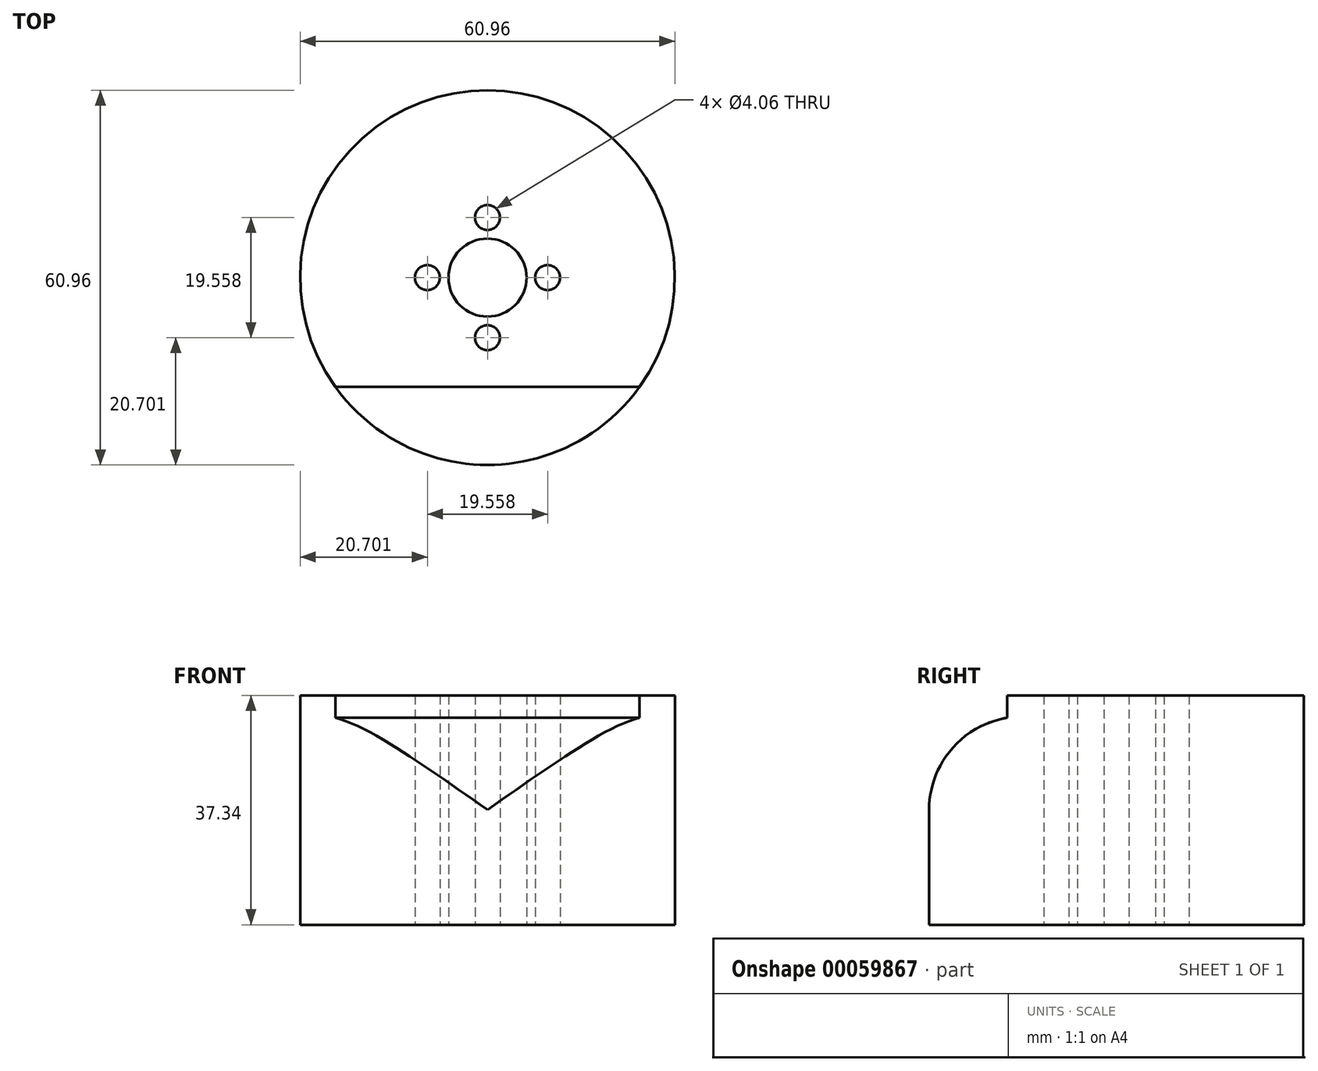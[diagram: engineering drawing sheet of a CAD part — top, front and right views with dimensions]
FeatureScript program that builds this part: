
annotation { "Feature Type Name" : "Feature", "Feature Type Description" : "" }
export const myFeature = defineFeature(function(context is Context, id is Id, definition is map)
    precondition{}
    {
        {
            var Q0;
            Q0=qCreatedBy(makeId("Top.planeOp"),FACE);
            var sketch = newSketch(context, id + "F0", { "sketchPlane" : qUnion([Q0])});
            skCircle(sketch, "E0", {"center": v(0, 0) * mm, "radius": 30.48 * mm});
            skCircle(sketch, "E1", {"center": v(0, 0) * mm, "radius": 6.35 * mm});
            skLineSegment(sketch, "E2", {"start": v(0, 0) * mm, "end": v(-9.78, 0) * mm});
            skLineSegment(sketch, "E3", {"start": v(0, 0) * mm, "end": v(9.78, 0) * mm});
            skLineSegment(sketch, "E4", {"start": v(0, 0) * mm, "end": v(0, -9.78) * mm});
            skLineSegment(sketch, "E5", {"start": v(0, 0) * mm, "end": v(0, 9.78) * mm});
            skCircle(sketch, "E6", {"center": v(-9.78, 0) * mm, "radius": 2.03 * mm});
            skCircle(sketch, "E7", {"center": v(0, 9.78) * mm, "radius": 2.03 * mm});
            skCircle(sketch, "E8", {"center": v(9.78, 0) * mm, "radius": 2.03 * mm});
            skCircle(sketch, "E9", {"center": v(0, -9.78) * mm, "radius": 2.03 * mm});
            skSolve(sketch);
        }
        {
            var Q0;
            Q0 = qSketchRegion(id + "F0", true);
            extrude(context, id + "F1", {"entities" : qUnion([Q0]), "depth" : 37.34 * mm});
        }
        {
            var Q0;
            Q0=qCreatedBy(makeId("Right.planeOp"),FACE);
            var sketch = newSketch(context, id + "F2", { "sketchPlane" : qUnion([Q0])});
            skPoint(sketch, "E10.endSnap0", {"position": v(5.2, -10.74) * mm});
            skLineSegment(sketch, "E10", {"start": v(5.2, -10.74) * mm, "end": v(17.9, -10.74) * mm});
            skLineSegment(sketch, "E11", {"start": v(5.2, 8.56) * mm, "end": v(5.2, 4.24) * mm});
            skLineSegment(sketch, "E12", {"start": v(5.2, 4.24) * mm, "end": v(5.2, -25.73) * mm});
            skLineSegment(sketch, "E13", {"start": v(0, 0) * mm, "end": v(-30.48, 0) * mm});
            skLineSegment(sketch, "E14", {"start": v(-30.48, 0) * mm, "end": v(-30.48, 37.4) * mm});
            skLineSegment(sketch, "E15", {"start": v(-30.48, 37.4) * mm, "end": v(0, 37.4) * mm});
            skLineSegment(sketch, "E16", {"start": v(-30.48, 18.7) * mm, "end": v(-17.78, 18.7) * mm});
            skPoint(sketch, "E16.endSnap0", {"position": v(-30.48, 18.7) * mm});
            skLineSegment(sketch, "E17", {"start": v(-17.78, 18.7) * mm, "end": v(-17.78, 33.68) * mm});
            skLineSegment(sketch, "E18", {"start": v(-17.78, 33.68) * mm, "end": v(-17.78, 3.71) * mm});
            skArc(sketch, "E19", {"start": v(-17.78, 33.68) * mm, "mid": v(-30.48, 18.7) * mm, "end": v(-17.78, 3.71) * mm});
            skLineSegment(sketch, "E20", {"start": v(-17.78, 33.68) * mm, "end": v(-17.78, 37.4) * mm});
            skLineSegment(sketch, "E21", {"start": v(-17.78, 37.4) * mm, "end": v(-30.48, 37.4) * mm});
            skLineSegment(sketch, "E22", {"start": v(-30.48, 0) * mm, "end": v(-17.78, 0) * mm});
            skLineSegment(sketch, "E23", {"start": v(-17.78, 0) * mm, "end": v(-17.78, 3.71) * mm});
            skSolve(sketch);
        }
        {
            var Q0;
            {var subQ4=sQuery(id+"F2.wireOp",EDGE,"E20");Q0=makeQuery(id+"F2.imprint","IMPRINT",FACE,{"disambiguationData":[TD([[makeQuery(id+"F2.imprint","IMPRINT",EDGE,{"derivedFrom":subQ4}),1.0]])]});}
            var Q1;
            {var subQ0=sQuery(id+"F2.wireOp",EDGE,"E22");Q1=makeQuery(id+"F2.imprint","IMPRINT",FACE,{"disambiguationData":[TD([[makeQuery(id+"F2.imprint","IMPRINT",EDGE,{"derivedFrom":subQ0}),1.0]])]});}
            extrude(context, id + "F3", {"entities" : qUnion([Q0, Q1]), "operationType" : NewBodyOperationType.REMOVE, "oppositeDirection" : true, "depth" : 39.58 * mm});
        }
        {
            var Q0;
            {var subQ4=sQuery(id+"F2.wireOp",EDGE,"E20");Q0=makeQuery(id+"F2.imprint","IMPRINT",FACE,{"disambiguationData":[TD([[makeQuery(id+"F2.imprint","IMPRINT",EDGE,{"derivedFrom":subQ4}),1.0]])]});}
            var Q1;
            {var subQ0=sQuery(id+"F2.wireOp",EDGE,"E22");Q1=makeQuery(id+"F2.imprint","IMPRINT",FACE,{"disambiguationData":[TD([[makeQuery(id+"F2.imprint","IMPRINT",EDGE,{"derivedFrom":subQ0}),1.0]])]});}
            extrude(context, id + "F4", {"entities" : qUnion([Q0, Q1]), "operationType" : NewBodyOperationType.REMOVE, "depth" : 55.88 * mm});
        }
    });
